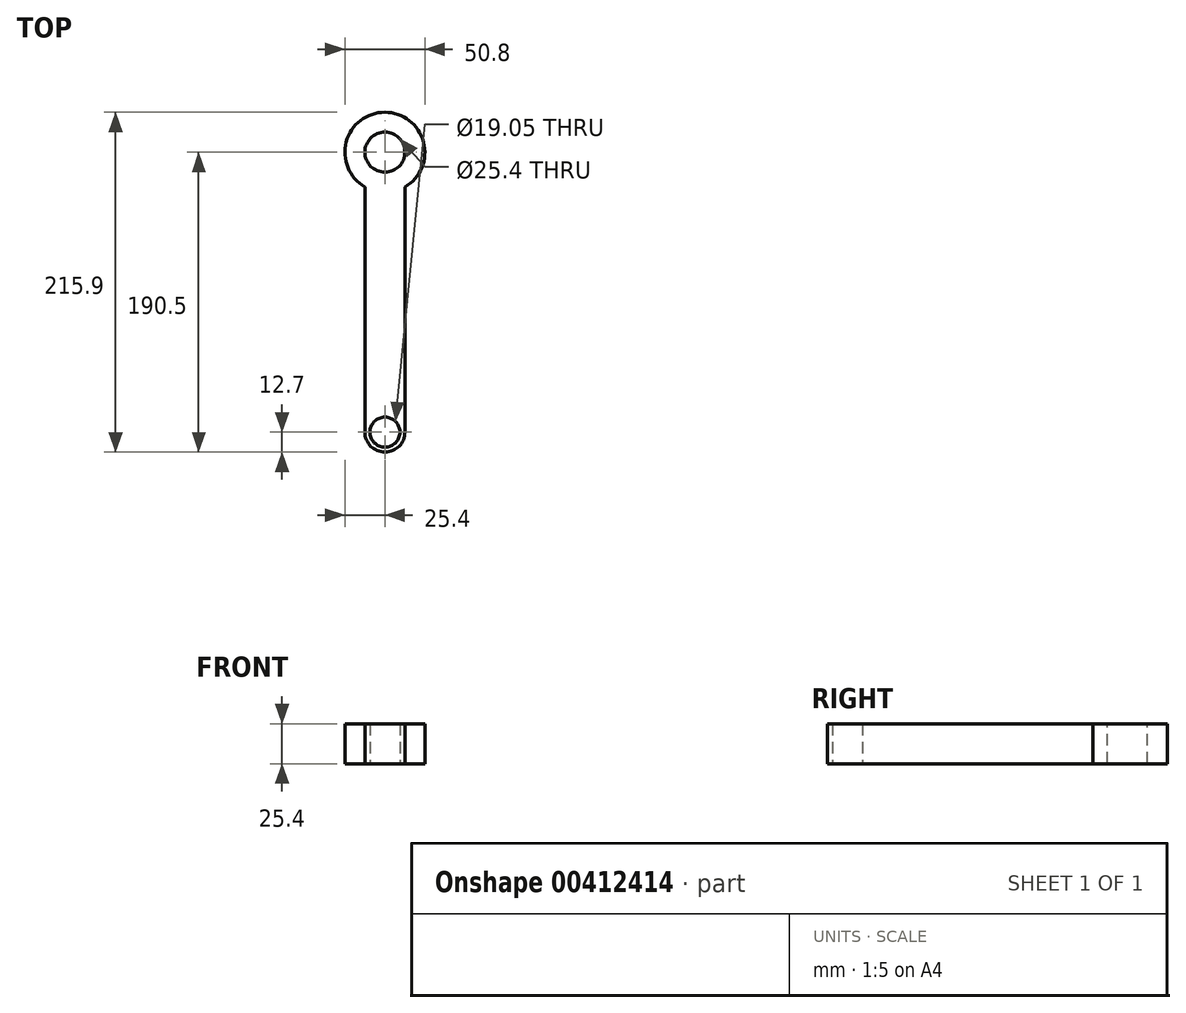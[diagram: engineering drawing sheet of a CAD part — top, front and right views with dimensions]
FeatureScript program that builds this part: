
annotation { "Feature Type Name" : "Feature", "Feature Type Description" : "" }
export const myFeature = defineFeature(function(context is Context, id is Id, definition is map)
    precondition{}
    {
        {
            var Q0;
            Q0=qCreatedBy(makeId("Top.planeOp"),FACE);
            var sketch = newSketch(context, id + "F0", { "sketchPlane" : qUnion([Q0])});
            skCircle(sketch, "E0", {"center": v(0, 0) * mm, "radius": 9.53 * mm});
            skCircle(sketch, "E1", {"center": v(0, 0) * mm, "radius": 12.7 * mm});
            skLineSegment(sketch, "E2", {"start": v(-12.7, 0) * mm, "end": v(-12.7, 177.8) * mm});
            skLineSegment(sketch, "E3", {"start": v(12.7, 0) * mm, "end": v(12.7, 177.8) * mm});
            skLineSegment(sketch, "E4", {"start": v(-12.7, 177.8) * mm, "end": v(12.7, 177.8) * mm});
            skSolve(sketch);
        }
        {
            var Q0;
            Q0 = qSketchRegion(id + "F0", true);
            extrude(context, id + "F1", {"entities" : qUnion([Q0]), "depth" : 25.4 * mm});
        }
        {
            var Q0;
            Q0=makeQuery(id+"F1.opExtrude","CAP_FACE",FACE,{"disambiguationData":[OSD([sQuery(id+"F0.wireOp",EDGE,"E0"),sQuery(id+"F0.wireOp",EDGE,"E1"),sQuery(id+"F0.wireOp",EDGE,"E2"),sQuery(id+"F0.wireOp",EDGE,"E3"),sQuery(id+"F0.wireOp",EDGE,"E4")])],"isStart":false});
            var sketch = newSketch(context, id + "F2", { "sketchPlane" : qUnion([Q0])});
            skCircle(sketch, "E5", {"center": v(0, 177.8) * mm, "radius": 25.4 * mm});
            skSolve(sketch);
        }
        {
            var Q0;
            Q0 = qSketchRegion(id + "F2", true);
            extrude(context, id + "F3", {"entities" : qUnion([Q0]), "operationType" : NewBodyOperationType.ADD, "oppositeDirection" : true, "depth" : 25.4 * mm});
        }
        {
            var Q0;
            Q0=makeQuery(id+"F3.boolean.opBoolean","MERGE",FACE,{"derivedFrom":[makeQuery(id+"F1.opExtrude","CAP_FACE",FACE,{"disambiguationData":[OSD([sQuery(id+"F0.wireOp",EDGE,"E0"),sQuery(id+"F0.wireOp",EDGE,"E1"),sQuery(id+"F0.wireOp",EDGE,"E2"),sQuery(id+"F0.wireOp",EDGE,"E3"),sQuery(id+"F0.wireOp",EDGE,"E4")])],"isStart":false}),makeQuery(id+"F3.opExtrude","CAP_FACE",FACE,{"disambiguationData":[OSD([sQuery(id+"F2.wireOp",EDGE,"E5")])],"isStart":true})]});
            var sketch = newSketch(context, id + "F4", { "sketchPlane" : qUnion([Q0])});
            skCircle(sketch, "E6", {"center": v(0, 177.8) * mm, "radius": 12.7 * mm});
            skSolve(sketch);
        }
        {
            var Q0;
            Q0 = qSketchRegion(id + "F4", true);
            extrude(context, id + "F5", {"entities" : qUnion([Q0]), "operationType" : NewBodyOperationType.REMOVE, "oppositeDirection" : true, "depth" : 25.4 * mm});
        }
    });
